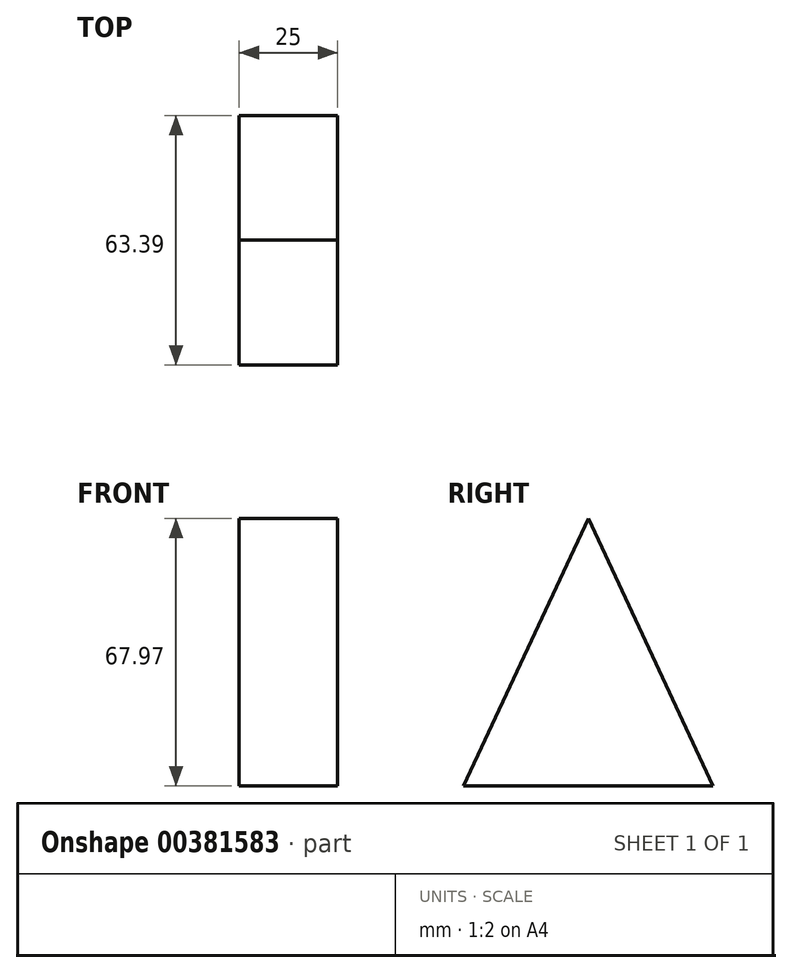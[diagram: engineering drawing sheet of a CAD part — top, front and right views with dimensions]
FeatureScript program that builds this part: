
annotation { "Feature Type Name" : "Feature", "Feature Type Description" : "" }
export const myFeature = defineFeature(function(context is Context, id is Id, definition is map)
    precondition{}
    {
        {
            var Q0;
            Q0=qCreatedBy(makeId("Right.planeOp"),FACE);
            var sketch = newSketch(context, id + "F0", { "sketchPlane" : qUnion([Q0])});
            skLineSegment(sketch, "E0", {"start": v(0, 0) * mm, "end": v(31.7, 67.97) * mm});
            skLineSegment(sketch, "E1", {"start": v(31.7, 67.97) * mm, "end": v(63.4, 0) * mm});
            skLineSegment(sketch, "E2", {"start": v(63.4, 0) * mm, "end": v(0, 0) * mm});
            skSolve(sketch);
        }
        {
            var Q0;
            Q0=makeQuery(id+"F0.imprint","IMPRINT",FACE,{"disambiguationData":[TD([[makeQuery(id+"F0.imprint","IMPRINT",EDGE,{"derivedFrom":sQuery(id+"F0.wireOp",EDGE,"E0")}),-1.0]])]});
            extrude(context, id + "F1", {"entities" : qUnion([Q0]), "depth" : 25 * mm, "offsetDistance" : 25 * mm});
        }
    });
